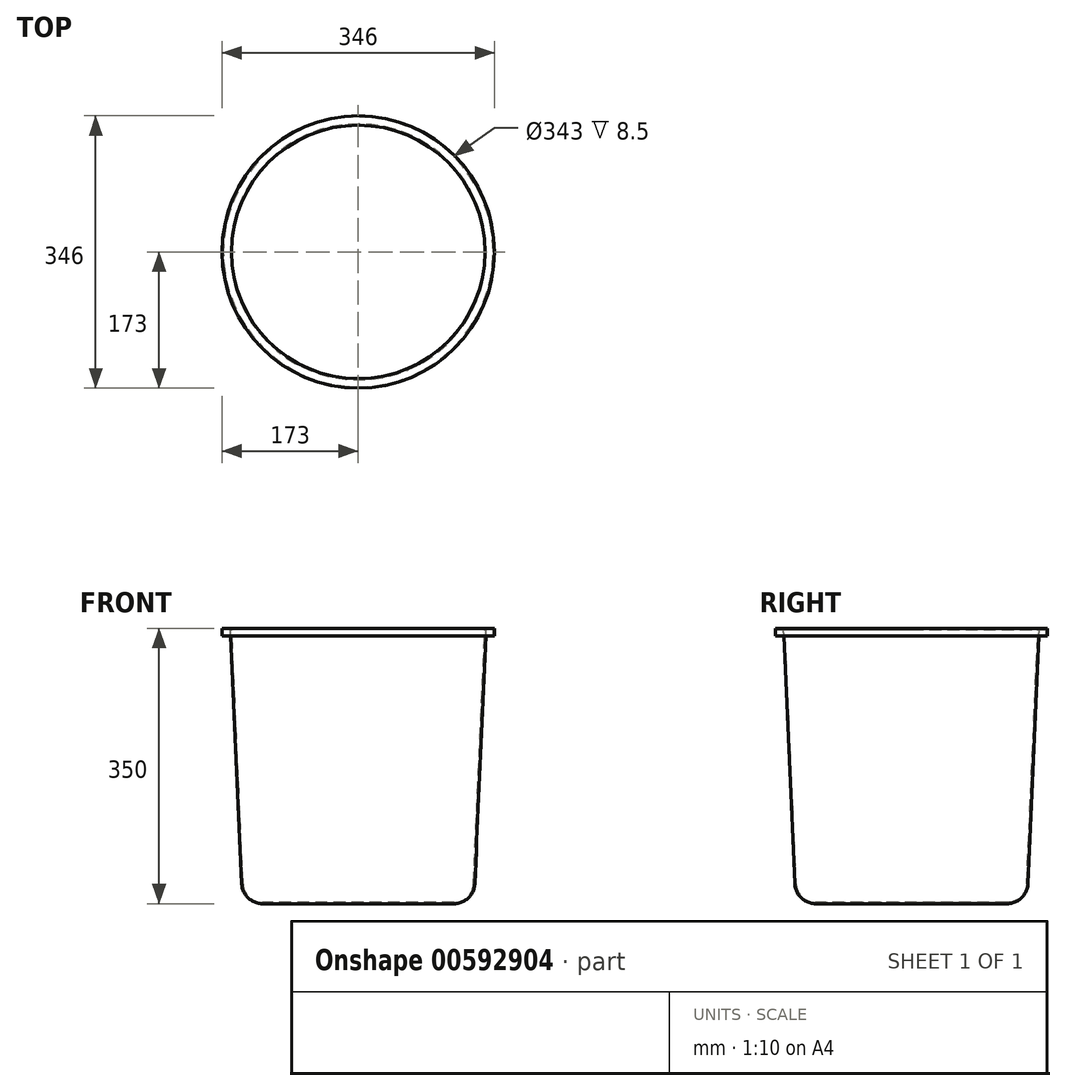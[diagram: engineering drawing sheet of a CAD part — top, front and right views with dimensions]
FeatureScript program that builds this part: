
annotation { "Feature Type Name" : "Feature", "Feature Type Description" : "" }
export const myFeature = defineFeature(function(context is Context, id is Id, definition is map)
    precondition{}
    {
        {
            var Q0;
            Q0=qCreatedBy(makeId("Front.planeOp"),FACE);
            var sketch = newSketch(context, id + "F0", { "sketchPlane" : qUnion([Q0])});
            skLineSegment(sketch, "E0", {"start": v(0, -10) * mm, "end": v(0, 0) * mm});
            skLineSegment(sketch, "E1", {"start": v(12, 0) * mm, "end": v(26.43, -324.61) * mm});
            skLineSegment(sketch, "E2", {"start": v(51.4, -348.5) * mm, "end": v(173, -348.5) * mm});
            skLineSegment(sketch, "E3", {"start": v(0, 0) * mm, "end": v(12, 0) * mm});
            skArc(sketch, "E4.filletArc", {"start": v(26.43, -324.61) * mm, "mid": v(34.12, -341.57) * mm, "end": v(51.4, -348.5) * mm});
            skLineSegment(sketch, "E5.0", {"start": v(51.4, -350) * mm, "end": v(173, -350) * mm});
            skLineSegment(sketch, "E5.1", {"start": v(1.5, -10) * mm, "end": v(1.5, -1.5) * mm});
            skLineSegment(sketch, "E5.2", {"start": v(1.5, -1.5) * mm, "end": v(10.57, -1.5) * mm});
            skLineSegment(sketch, "E5.3", {"start": v(10.57, -1.5) * mm, "end": v(24.93, -324.68) * mm});
            skArc(sketch, "E5.4", {"start": v(24.93, -324.68) * mm, "mid": v(33.09, -342.65) * mm, "end": v(51.4, -350) * mm});
            skLineSegment(sketch, "E6", {"start": v(173, -348.5) * mm, "end": v(173, -350) * mm});
            skLineSegment(sketch, "E7", {"start": v(0, -10) * mm, "end": v(1.5, -10) * mm});
            skSolve(sketch);
        }
        {
            var Q0;
            Q0 = qSketchRegion(id + "F0", true);
            var Q1;
            Q1=sQuery(id+"F0.wireOp",EDGE,"E6");
            revolve(context, id + "F1", {"entities" : qUnion([Q0]), "axis" : qUnion([Q1]), "revolveType" : RevolveType.FULL});
        }
    });
